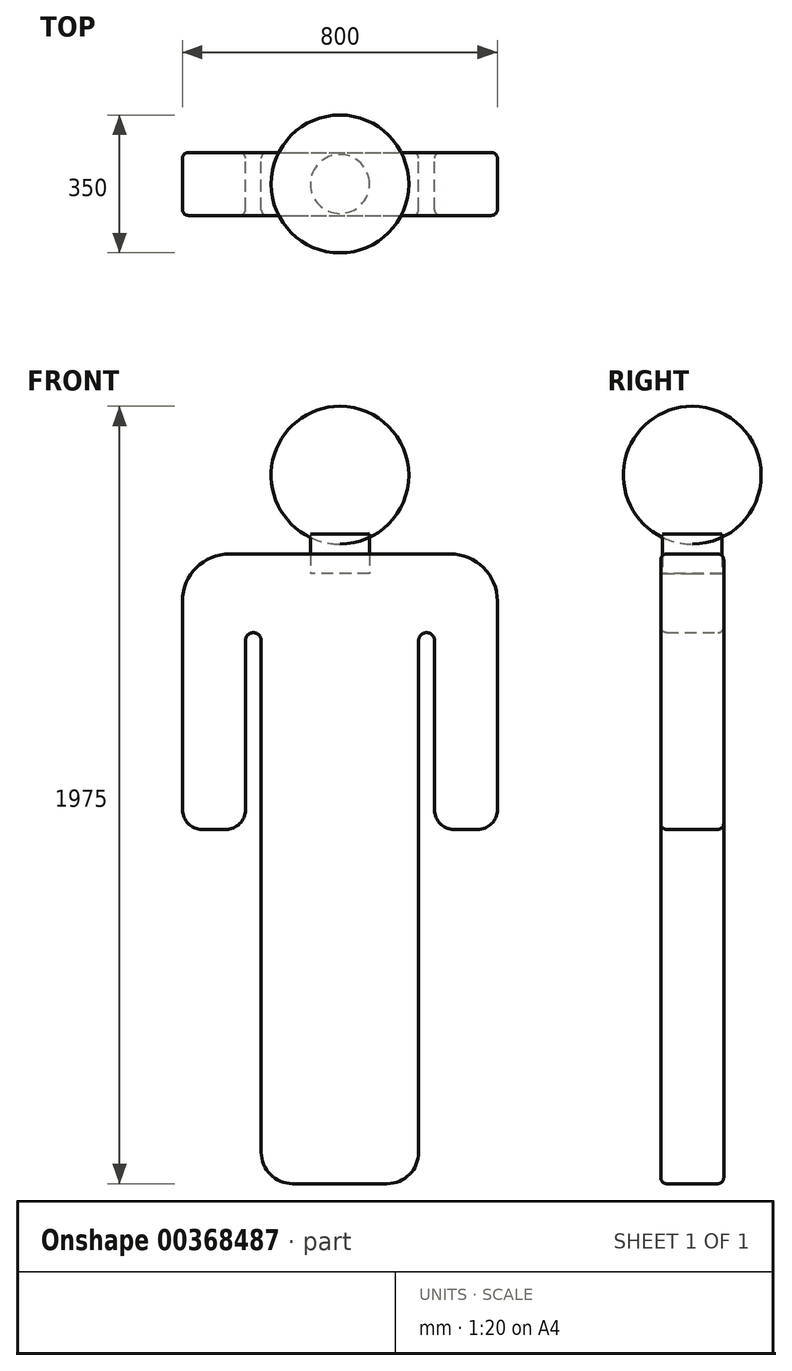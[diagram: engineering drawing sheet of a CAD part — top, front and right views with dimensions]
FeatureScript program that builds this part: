
annotation { "Feature Type Name" : "Feature", "Feature Type Description" : "" }
export const myFeature = defineFeature(function(context is Context, id is Id, definition is map)
    precondition{}
    {
        {
            var Q0;
            Q0=qCreatedBy(makeId("Front.planeOp"),FACE);
            var sketch = newSketch(context, id + "F0", { "sketchPlane" : qUnion([Q0])});
            skLineSegment(sketch, "E0.bottom", {"start": v(-306.67, 700) * mm, "end": v(93.33, 700) * mm});
            skLineSegment(sketch, "E0.top", {"start": v(-306.67, -900) * mm, "end": v(93.33, -900) * mm});
            skLineSegment(sketch, "E0.left", {"start": v(-306.67, 700) * mm, "end": v(-306.67, -900) * mm});
            skLineSegment(sketch, "E0.right", {"start": v(93.33, 700) * mm, "end": v(93.33, -900) * mm});
            skLineSegment(sketch, "E1.bottom", {"start": v(-506.67, 700) * mm, "end": v(293.33, 700) * mm});
            skLineSegment(sketch, "E1.top", {"start": v(-506.67, 500) * mm, "end": v(293.33, 500) * mm});
            skLineSegment(sketch, "E1.left", {"start": v(-506.67, 700) * mm, "end": v(-506.67, 500) * mm});
            skLineSegment(sketch, "E1.right", {"start": v(293.33, 700) * mm, "end": v(293.33, 500) * mm});
            skLineSegment(sketch, "E2.bottom", {"start": v(-506.67, 500) * mm, "end": v(-346.67, 500) * mm});
            skLineSegment(sketch, "E2.top", {"start": v(-506.67, 0) * mm, "end": v(-346.67, 0) * mm});
            skLineSegment(sketch, "E2.left", {"start": v(-506.67, 500) * mm, "end": v(-506.67, 0) * mm});
            skLineSegment(sketch, "E2.right", {"start": v(-346.67, 500) * mm, "end": v(-346.67, 0) * mm});
            skLineSegment(sketch, "E3.bottom", {"start": v(293.33, 500) * mm, "end": v(133.33, 500) * mm});
            skLineSegment(sketch, "E3.top", {"start": v(293.33, 0) * mm, "end": v(133.33, 0) * mm});
            skLineSegment(sketch, "E3.left", {"start": v(293.33, 500) * mm, "end": v(293.33, 0) * mm});
            skLineSegment(sketch, "E3.right", {"start": v(133.33, 500) * mm, "end": v(133.33, 0) * mm});
            skSolve(sketch);
        }
        {
            var Q0;
            Q0 = qSketchRegion(id + "F0", true);
            extrude(context, id + "F1", {"entities" : qUnion([Q0]), "endBound" : BoundingType.SYMMETRIC, "depth" : 160 * mm});
        }
        {
            var Q0;
            Q0=makeQuery(id+"F1.opExtrude","SWEPT_EDGE",EDGE,{"disambiguationData":[OSD([sQuery(id+"F0.wireOp",EDGE,"E1.bottom"),sQuery(id+"F0.wireOp",EDGE,"E1.right")])]});
            var Q1;
            Q1=makeQuery(id+"F1.opExtrude","SWEPT_EDGE",EDGE,{"disambiguationData":[OSD([sQuery(id+"F0.wireOp",EDGE,"E1.bottom"),sQuery(id+"F0.wireOp",EDGE,"E1.left")])]});
            fillet(context, id + "F2", {"entities" : qUnion([Q0, Q1]), "radius" : 120 * mm, "tangentPropagation" : true, "allowEdgeOverflow" : false});
        }
        {
            var Q0;
            Q0=makeQuery(id+"F1.opExtrude","SWEPT_EDGE",EDGE,{"disambiguationData":[OSD([sQuery(id+"F0.wireOp",EDGE,"E3.top"),sQuery(id+"F0.wireOp",EDGE,"E3.left")])]});
            var Q1;
            Q1=makeQuery(id+"F1.opExtrude","SWEPT_EDGE",EDGE,{"disambiguationData":[OSD([sQuery(id+"F0.wireOp",EDGE,"E2.top"),sQuery(id+"F0.wireOp",EDGE,"E2.right")])]});
            var Q2;
            Q2=makeQuery(id+"F1.opExtrude","SWEPT_EDGE",EDGE,{"disambiguationData":[OSD([sQuery(id+"F0.wireOp",EDGE,"E3.top"),sQuery(id+"F0.wireOp",EDGE,"E3.right")])]});
            var Q3;
            Q3=makeQuery(id+"F1.opExtrude","SWEPT_EDGE",EDGE,{"disambiguationData":[OSD([sQuery(id+"F0.wireOp",EDGE,"E2.top"),sQuery(id+"F0.wireOp",EDGE,"E2.left")])]});
            fillet(context, id + "F3", {"entities" : qUnion([Q0, Q1, Q2, Q3]), "radius" : 50 * mm, "tangentPropagation" : true, "allowEdgeOverflow" : false});
        }
        {
            var Q0;
            Q0=makeQuery(id+"F1.opExtrude","SWEPT_EDGE",EDGE,{"disambiguationData":[OSD([sQuery(id+"F0.wireOp",EDGE,"E1.top"),sQuery(id+"F0.wireOp",EDGE,"E2.bottom"),sQuery(id+"F0.wireOp",EDGE,"E2.right")])]});
            var Q1;
            Q1=makeQuery(id+"F1.opExtrude","SWEPT_EDGE",EDGE,{"disambiguationData":[OSD([sQuery(id+"F0.wireOp",EDGE,"E0.right"),sQuery(id+"F0.wireOp",EDGE,"E1.top")])]});
            var Q2;
            Q2=makeQuery(id+"F1.opExtrude","SWEPT_EDGE",EDGE,{"disambiguationData":[OSD([sQuery(id+"F0.wireOp",EDGE,"E0.left"),sQuery(id+"F0.wireOp",EDGE,"E1.top")])]});
            var Q3;
            Q3=makeQuery(id+"F1.opExtrude","SWEPT_EDGE",EDGE,{"disambiguationData":[OSD([sQuery(id+"F0.wireOp",EDGE,"E1.top"),sQuery(id+"F0.wireOp",EDGE,"E3.bottom"),sQuery(id+"F0.wireOp",EDGE,"E3.right")])]});
            fillet(context, id + "F4", {"entities" : qUnion([Q0, Q1, Q2, Q3]), "radius" : 20 * mm, "tangentPropagation" : true, "allowEdgeOverflow" : false});
        }
        {
            var Q0;
            Q0=makeQuery(id+"F1.opExtrude","SWEPT_EDGE",EDGE,{"disambiguationData":[OSD([sQuery(id+"F0.wireOp",EDGE,"E0.top"),sQuery(id+"F0.wireOp",EDGE,"E0.left")])]});
            var Q1;
            Q1=makeQuery(id+"F1.opExtrude","SWEPT_EDGE",EDGE,{"disambiguationData":[OSD([sQuery(id+"F0.wireOp",EDGE,"E0.top"),sQuery(id+"F0.wireOp",EDGE,"E0.right")])]});
            fillet(context, id + "F5", {"entities" : qUnion([Q0, Q1]), "radius" : 80 * mm, "tangentPropagation" : true, "allowEdgeOverflow" : false});
        }
        {
            var Q0;
            Q0=makeQuery(id+"F1.opExtrude","CAP_EDGE",EDGE,{"disambiguationData":[OSD([sQuery(id+"F0.wireOp",EDGE,"E1.bottom")])],"isStart":false});
            var Q1;
            Q1=makeQuery(id+"F1.opExtrude","CAP_EDGE",EDGE,{"disambiguationData":[OSD([sQuery(id+"F0.wireOp",EDGE,"E0.right")])],"isStart":true});
            fillet(context, id + "F6", {"entities" : qUnion([Q0, Q1]), "radius" : 15 * mm, "tangentPropagation" : true, "allowEdgeOverflow" : false});
        }
        {
            var Q0;
            Q0=qCreatedBy(makeId("Front.planeOp"),FACE);
            var sketch = newSketch(context, id + "F7", { "sketchPlane" : qUnion([Q0])});
            skCircle(sketch, "E4", {"center": v(-106.67, 900) * mm, "radius": 175 * mm});
            skLineSegment(sketch, "E5", {"start": v(-106.67, 725) * mm, "end": v(-106.67, 1075) * mm});
            skSolve(sketch);
        }
        {
            var Q0;
            {var subQ0=sQuery(id+"F7.wireOp",EDGE,"E5");Q0=makeQuery(id+"F7.imprint","IMPRINT",FACE,{"disambiguationData":[TD([[makeQuery(id+"F7.imprint","IMPRINT",EDGE,{"derivedFrom":subQ0}),-1.0]])]});}
            var Q1;
            Q1=sQuery(id+"F7.wireOp",EDGE,"E5");
            revolve(context, id + "F8", {"entities" : qUnion([Q0]), "axis" : qUnion([Q1]), "revolveType" : RevolveType.FULL});
        }
        {
            var Q0;
            Q0=makeQuery(id+"F1.opExtrude","SWEPT_FACE",FACE,{"disambiguationData":[OSD([sQuery(id+"F0.wireOp",EDGE,"E1.bottom")])]});
            var sketch = newSketch(context, id + "F9", { "sketchPlane" : qUnion([Q0])});
            skCircle(sketch, "E6", {"center": v(-106.67, 0) * mm, "radius": 75 * mm});
            skPoint(sketch, "E6.centerSnap0", {"position": v(-106.67, 65) * mm});
            skSolve(sketch);
        }
        {
            var Q0;
            Q0 = qSketchRegion(id + "F9", true);
            extrude(context, id + "F10", {"entities" : qUnion([Q0]), "endBound" : BoundingType.SYMMETRIC, "depth" : 100 * mm});
        }
    });
